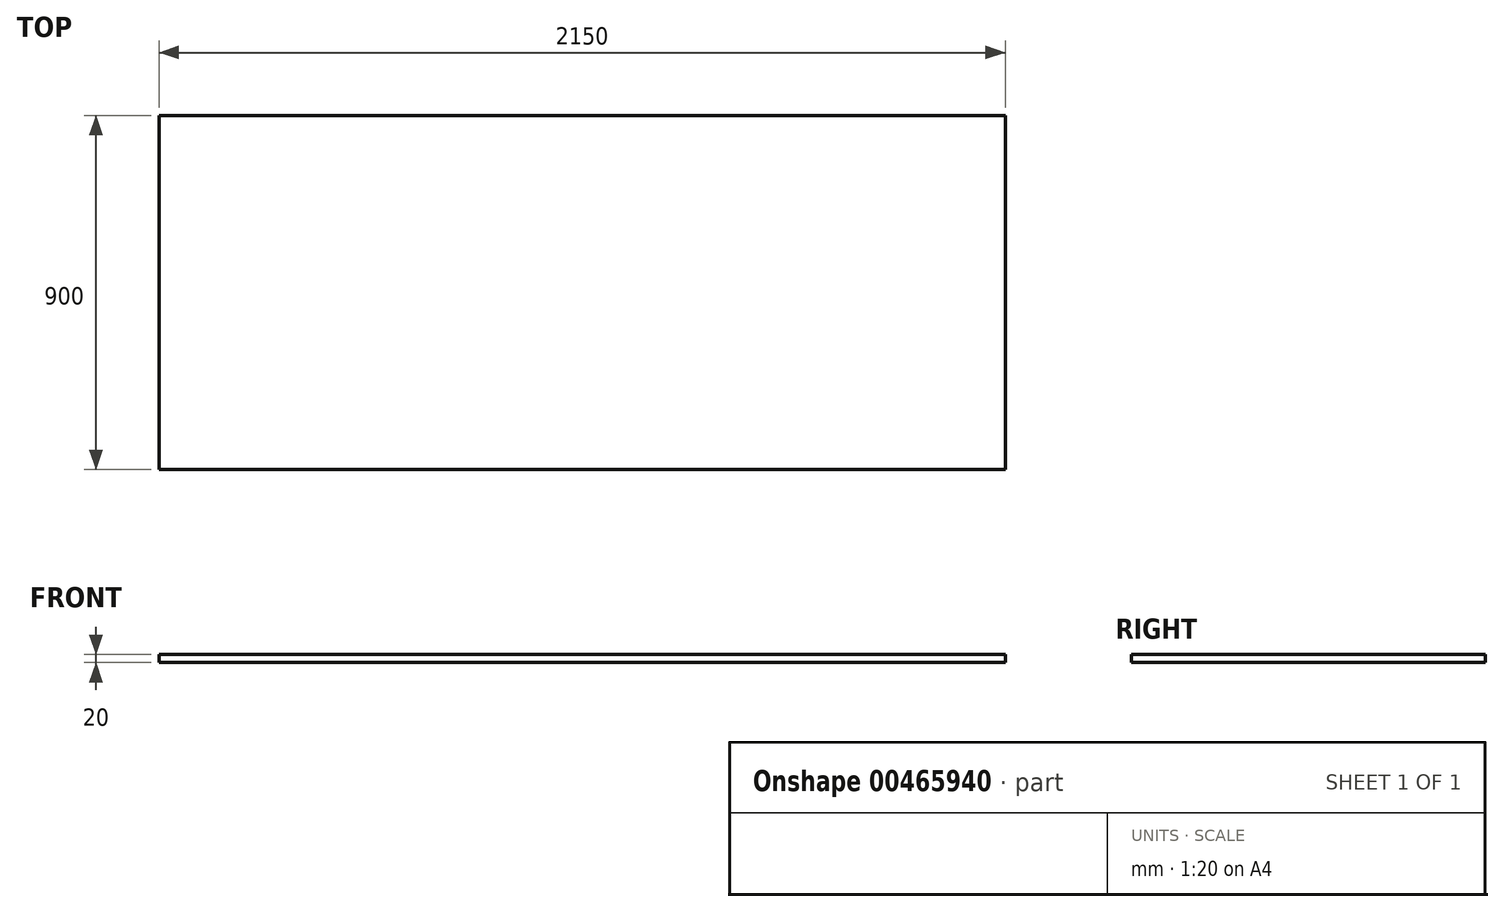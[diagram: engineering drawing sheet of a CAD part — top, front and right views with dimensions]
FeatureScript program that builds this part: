
annotation { "Feature Type Name" : "Feature", "Feature Type Description" : "" }
export const myFeature = defineFeature(function(context is Context, id is Id, definition is map)
    precondition{}
    {
        {
            var Q0;
            Q0=qCreatedBy(makeId("Top.planeOp"),FACE);
            var sketch = newSketch(context, id + "F0", { "sketchPlane" : qUnion([Q0])});
            skLineSegment(sketch, "E0.bottom", {"start": v(-1064.72, 125.7) * mm, "end": v(1085.28, 125.7) * mm});
            skLineSegment(sketch, "E0.top", {"start": v(-1064.72, -774.3) * mm, "end": v(1085.28, -774.3) * mm});
            skLineSegment(sketch, "E0.left", {"start": v(-1064.72, 125.7) * mm, "end": v(-1064.72, -774.3) * mm});
            skLineSegment(sketch, "E0.right", {"start": v(1085.28, 125.7) * mm, "end": v(1085.28, -774.3) * mm});
            skSolve(sketch);
        }
        {
            var Q0;
            Q0 = qSketchRegion(id + "F0", true);
            extrude(context, id + "F1", {"entities" : qUnion([Q0]), "depth" : 20 * mm});
        }
    });
